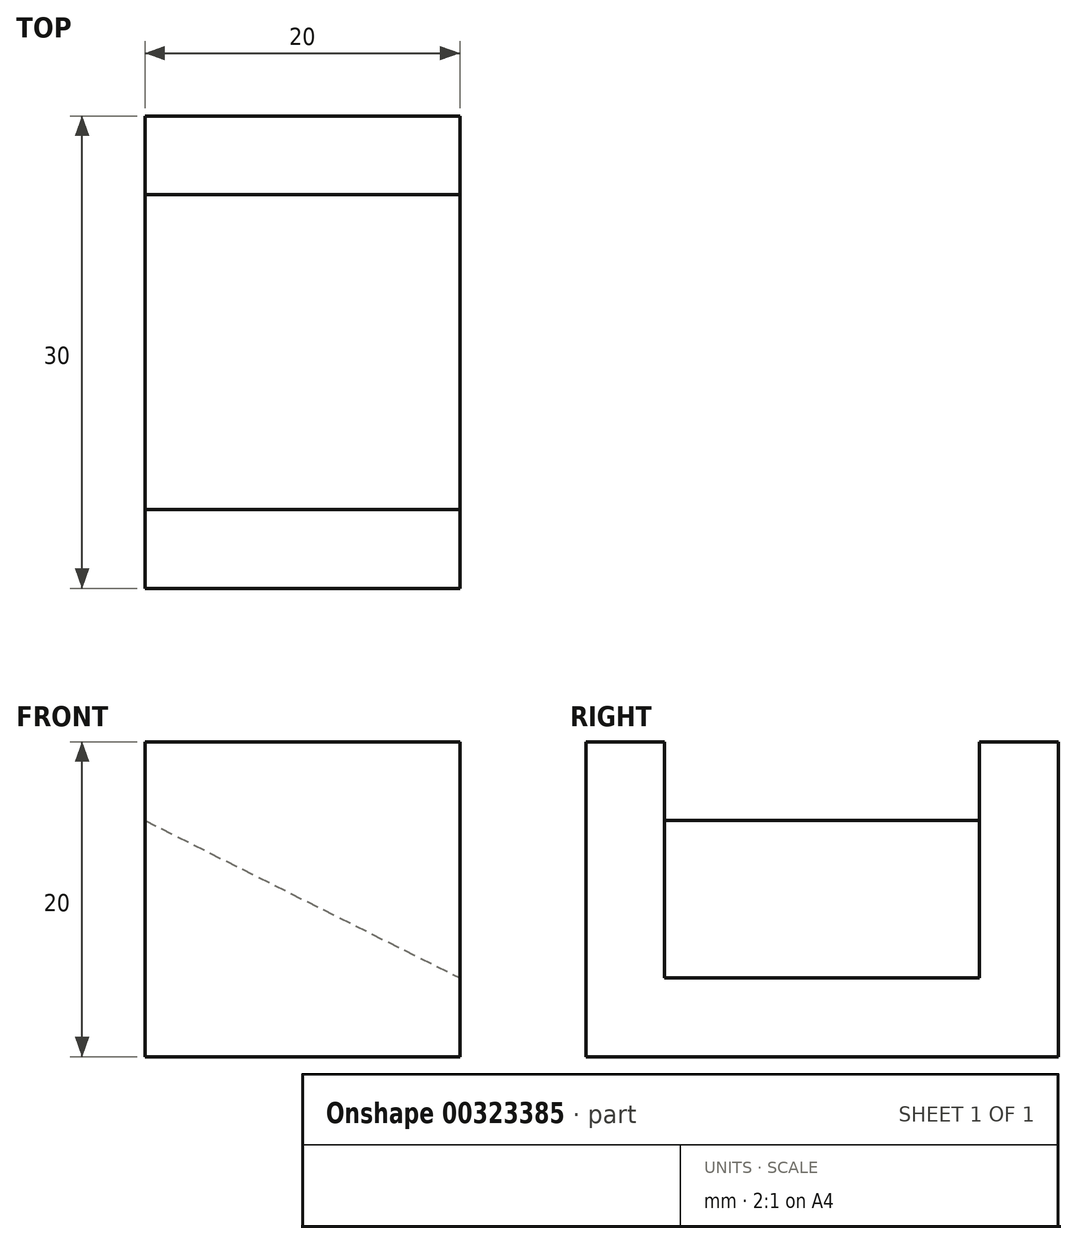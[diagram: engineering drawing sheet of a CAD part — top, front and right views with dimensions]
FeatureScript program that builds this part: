
annotation { "Feature Type Name" : "Feature", "Feature Type Description" : "" }
export const myFeature = defineFeature(function(context is Context, id is Id, definition is map)
    precondition{}
    {
        {
            var Q0;
            Q0=qCreatedBy(makeId("Front.planeOp"),FACE);
            var sketch = newSketch(context, id + "F0", { "sketchPlane" : qUnion([Q0])});
            skLineSegment(sketch, "E0", {"start": v(0, 0) * mm, "end": v(0, 5) * mm});
            skLineSegment(sketch, "E1", {"start": v(0, 5) * mm, "end": v(20, 5) * mm});
            skLineSegment(sketch, "E2", {"start": v(20, 5) * mm, "end": v(20, 0) * mm});
            skLineSegment(sketch, "E3", {"start": v(20, 0) * mm, "end": v(0, 0) * mm});
            skSolve(sketch);
        }
        {
            var Q0;
            Q0 = qSketchRegion(id + "F0", true);
            extrude(context, id + "F1", {"entities" : qUnion([Q0]), "endBound" : BoundingType.SYMMETRIC, "depth" : 30 * mm});
        }
        {
            var Q0;
            Q0=makeQuery(id+"F1.opExtrude","CAP_FACE",FACE,{"disambiguationData":[OSD([sQuery(id+"F0.wireOp",EDGE,"E0"),sQuery(id+"F0.wireOp",EDGE,"E1"),sQuery(id+"F0.wireOp",EDGE,"E2"),sQuery(id+"F0.wireOp",EDGE,"E3")])],"isStart":false});
            var sketch = newSketch(context, id + "F2", { "sketchPlane" : qUnion([Q0])});
            skLineSegment(sketch, "E4", {"start": v(0, 5) * mm, "end": v(0, 20) * mm});
            skLineSegment(sketch, "E5", {"start": v(20, 5) * mm, "end": v(20, 20) * mm});
            skLineSegment(sketch, "E6", {"start": v(20, 20) * mm, "end": v(0, 20) * mm});
            skLineSegment(sketch, "E7", {"start": v(0, 5) * mm, "end": v(20, 5) * mm});
            skSolve(sketch);
        }
        {
            var Q0;
            Q0 = qSketchRegion(id + "F2", true);
            extrude(context, id + "F3", {"entities" : qUnion([Q0]), "operationType" : NewBodyOperationType.ADD, "oppositeDirection" : true, "depth" : 5 * mm});
        }
        {
            var Q0;
            Q0=makeQuery(id+"F1.opExtrude","CAP_FACE",FACE,{"disambiguationData":[OSD([sQuery(id+"F0.wireOp",EDGE,"E0"),sQuery(id+"F0.wireOp",EDGE,"E1"),sQuery(id+"F0.wireOp",EDGE,"E2"),sQuery(id+"F0.wireOp",EDGE,"E3")])],"isStart":true});
            var sketch = newSketch(context, id + "F4", { "sketchPlane" : qUnion([Q0])});
            skLineSegment(sketch, "E8", {"start": v(-20, 5) * mm, "end": v(0, 5) * mm});
            skLineSegment(sketch, "E9", {"start": v(0, 5) * mm, "end": v(0, 15) * mm});
            skLineSegment(sketch, "E10", {"start": v(0, 15) * mm, "end": v(-20, 5) * mm});
            skSolve(sketch);
        }
        {
            var Q0;
            Q0 = qSketchRegion(id + "F4", true);
            extrude(context, id + "F5", {"entities" : qUnion([Q0]), "operationType" : NewBodyOperationType.ADD, "oppositeDirection" : true, "depth" : 25 * mm});
        }
        {
            var Q0;
            Q0=makeQuery(id+"F5.boolean.opBoolean","MERGE",FACE,{"derivedFrom":[makeQuery(id+"F1.opExtrude","CAP_FACE",FACE,{"disambiguationData":[OSD([sQuery(id+"F0.wireOp",EDGE,"E0"),sQuery(id+"F0.wireOp",EDGE,"E1"),sQuery(id+"F0.wireOp",EDGE,"E2"),sQuery(id+"F0.wireOp",EDGE,"E3")])],"isStart":true}),makeQuery(id+"F5.opExtrude","CAP_FACE",FACE,{"disambiguationData":[OSD([sQuery(id+"F4.wireOp",EDGE,"E8"),sQuery(id+"F4.wireOp",EDGE,"E9"),sQuery(id+"F4.wireOp",EDGE,"E10")])],"isStart":true})]});
            var sketch = newSketch(context, id + "F6", { "sketchPlane" : qUnion([Q0])});
            skLineSegment(sketch, "E11", {"start": v(-20, 5) * mm, "end": v(0, 5) * mm});
            skLineSegment(sketch, "E12", {"start": v(0, 5) * mm, "end": v(0, 15) * mm});
            skLineSegment(sketch, "E13", {"start": v(0, 15) * mm, "end": v(-20, 5) * mm});
            skSolve(sketch);
        }
        {
            var Q0;
            Q0 = qSketchRegion(id + "F6", true);
            extrude(context, id + "F7", {"entities" : qUnion([Q0]), "operationType" : NewBodyOperationType.REMOVE, "oppositeDirection" : true, "depth" : 5 * mm});
        }
        {
            var Q0;
            Q0=makeQuery(id+"F5.boolean.opBoolean","MERGE",FACE,{"derivedFrom":[makeQuery(id+"F1.opExtrude","CAP_FACE",FACE,{"disambiguationData":[OSD([sQuery(id+"F0.wireOp",EDGE,"E0"),sQuery(id+"F0.wireOp",EDGE,"E1"),sQuery(id+"F0.wireOp",EDGE,"E2"),sQuery(id+"F0.wireOp",EDGE,"E3")])],"isStart":true}),makeQuery(id+"F5.opExtrude","CAP_FACE",FACE,{"disambiguationData":[OSD([sQuery(id+"F4.wireOp",EDGE,"E8"),sQuery(id+"F4.wireOp",EDGE,"E9"),sQuery(id+"F4.wireOp",EDGE,"E10")])],"isStart":true})]});
            var sketch = newSketch(context, id + "F8", { "sketchPlane" : qUnion([Q0])});
            skLineSegment(sketch, "E14", {"start": v(-20, 5) * mm, "end": v(-20, 20) * mm});
            skLineSegment(sketch, "E15", {"start": v(-20, 20) * mm, "end": v(0, 20) * mm});
            skLineSegment(sketch, "E16", {"start": v(0, 20) * mm, "end": v(0, 5) * mm});
            skLineSegment(sketch, "E17", {"start": v(0, 5) * mm, "end": v(-20, 5) * mm});
            skSolve(sketch);
        }
        {
            var Q0;
            Q0 = qSketchRegion(id + "F8", true);
            extrude(context, id + "F9", {"entities" : qUnion([Q0]), "operationType" : NewBodyOperationType.ADD, "oppositeDirection" : true, "depth" : 5 * mm});
        }
    });
